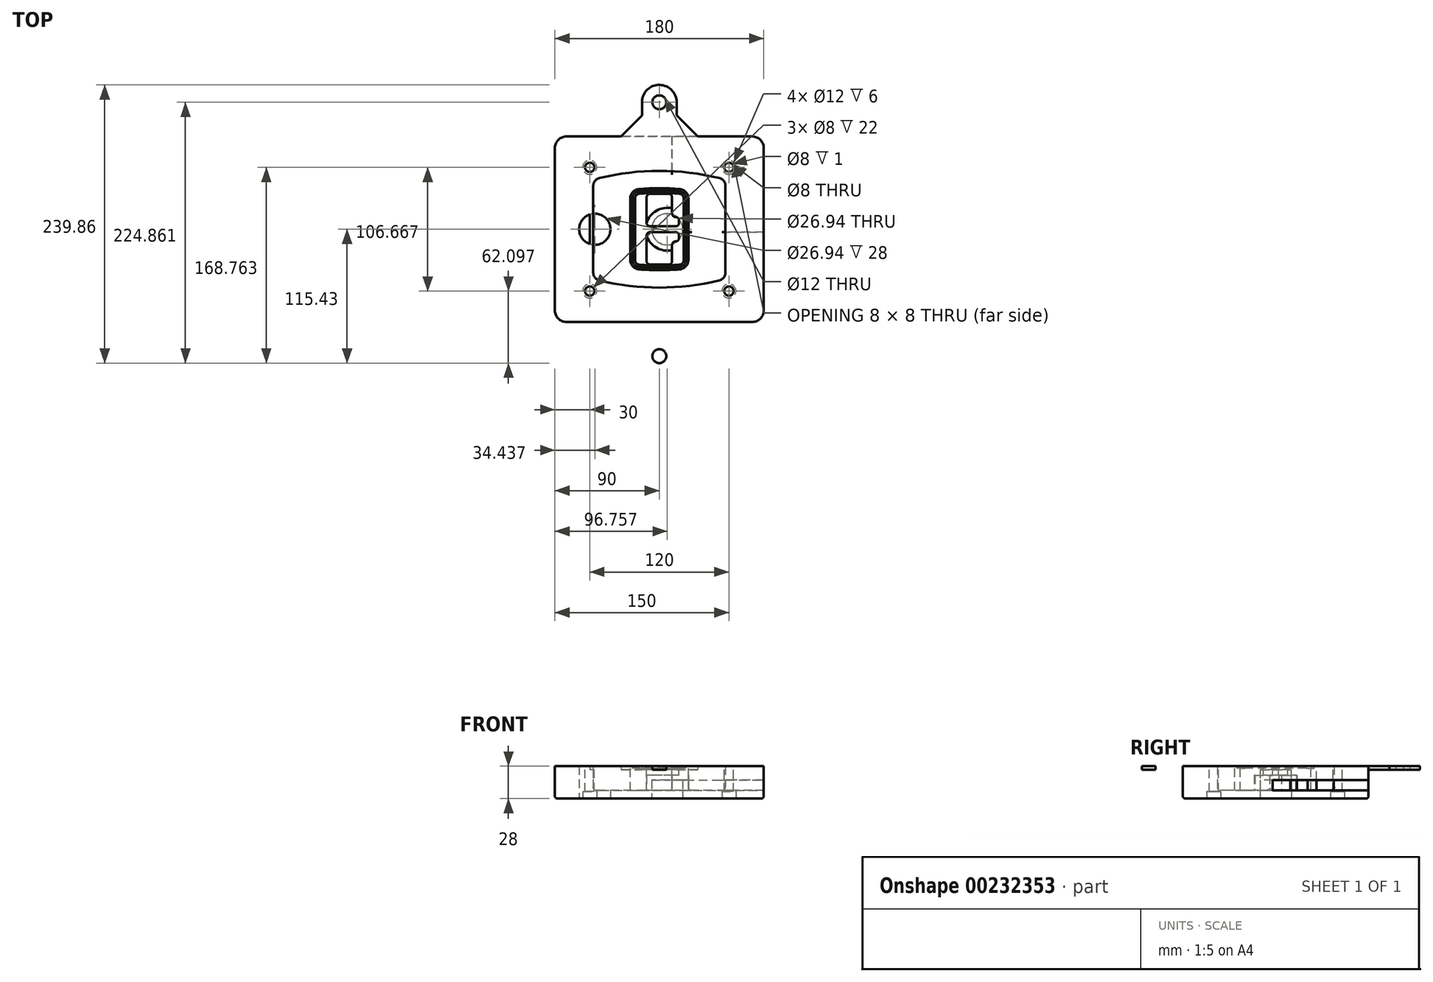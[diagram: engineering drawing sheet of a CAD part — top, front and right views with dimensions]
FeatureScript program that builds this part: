
annotation { "Feature Type Name" : "Feature", "Feature Type Description" : "" }
export const myFeature = defineFeature(function(context is Context, id is Id, definition is map)
    precondition{}
    {
        {
            var Q0;
            Q0=qCreatedBy(makeId("Top.planeOp"),FACE);
            var sketch = newSketch(context, id + "F0", { "sketchPlane" : qUnion([Q0])});
            skPoint(sketch, "E0.rect.middle", {"position": v(0, 0) * mm});
            skLineSegment(sketch, "E1.bottom", {"start": v(-80, -80) * mm, "end": v(80, -80) * mm});
            skLineSegment(sketch, "E1.top", {"start": v(-80, 80) * mm, "end": v(80, 80) * mm});
            skLineSegment(sketch, "E1.left", {"start": v(-90, -70) * mm, "end": v(-90, 70) * mm});
            skLineSegment(sketch, "E1.right", {"start": v(90, -70) * mm, "end": v(90, 70) * mm});
            skLineSegment(sketch, "E2", {"start": v(-90, 80) * mm, "end": v(90, -80) * mm, "construction": true});
            skLineSegment(sketch, "E3", {"start": v(90, 80) * mm, "end": v(-90, -80) * mm, "construction": true});
            skCircle(sketch, "E4", {"center": v(-60, 53.33) * mm, "radius": 4 * mm});
            skCircle(sketch, "E5", {"center": v(60, 53.33) * mm, "radius": 4 * mm});
            skCircle(sketch, "E6", {"center": v(60, -53.33) * mm, "radius": 4 * mm});
            skCircle(sketch, "E7", {"center": v(-60, -53.33) * mm, "radius": 4 * mm});
            skLineSegment(sketch, "E8", {"start": v(-60, 53.33) * mm, "end": v(60, 53.33) * mm, "construction": true});
            skLineSegment(sketch, "E9", {"start": v(60, 53.33) * mm, "end": v(60, -53.33) * mm, "construction": true});
            skLineSegment(sketch, "E10", {"start": v(60, -53.33) * mm, "end": v(-60, -53.33) * mm, "construction": true});
            skLineSegment(sketch, "E11", {"start": v(-60, -53.33) * mm, "end": v(-60, 53.33) * mm, "construction": true});
            skLineSegment(sketch, "E12", {"start": v(-60, 37.3) * mm, "end": v(-60, -37.3) * mm});
            skLineSegment(sketch, "E13", {"start": v(60, 37.3) * mm, "end": v(60, -37.3) * mm});
            skArc(sketch, "E14", {"start": v(52.38, 47.01) * mm, "mid": v(0, 53.33) * mm, "end": v(-52.38, 47.01) * mm});
            skArc(sketch, "E15", {"start": v(-52.38, -47.01) * mm, "mid": v(0, -53.33) * mm, "end": v(52.38, -47.01) * mm});
            skLineSegment(sketch, "E16", {"start": v(-60, 0) * mm, "end": v(60, 0) * mm, "construction": true});
            skPoint(sketch, "E17.visualSharp", {"position": v(-60, -45) * mm});
            skArc(sketch, "E17.filletArc", {"start": v(-60, -37.3) * mm, "mid": v(-57.87, -43.47) * mm, "end": v(-52.38, -47.01) * mm});
            skPoint(sketch, "E18.visualSharp", {"position": v(-60, 45) * mm});
            skArc(sketch, "E18.filletArc", {"start": v(-52.38, 47.01) * mm, "mid": v(-57.87, 43.47) * mm, "end": v(-60, 37.3) * mm});
            skPoint(sketch, "E19.visualSharp", {"position": v(60, 45) * mm});
            skArc(sketch, "E19.filletArc", {"start": v(60, 37.3) * mm, "mid": v(57.87, 43.47) * mm, "end": v(52.38, 47.01) * mm});
            skPoint(sketch, "E20.visualSharp", {"position": v(60, -45) * mm});
            skArc(sketch, "E20.filletArc", {"start": v(52.38, -47.01) * mm, "mid": v(57.87, -43.47) * mm, "end": v(60, -37.3) * mm});
            skPoint(sketch, "E21.visualSharp", {"position": v(-90, 80) * mm});
            skArc(sketch, "E21.filletArc", {"start": v(-80, 80) * mm, "mid": v(-87.07, 77.07) * mm, "end": v(-90, 70) * mm});
            skPoint(sketch, "E22.visualSharp", {"position": v(90, 80) * mm});
            skArc(sketch, "E22.filletArc", {"start": v(90, 70) * mm, "mid": v(87.07, 77.07) * mm, "end": v(80, 80) * mm});
            skPoint(sketch, "E23.visualSharp", {"position": v(90, -80) * mm});
            skArc(sketch, "E23.filletArc", {"start": v(80, -80) * mm, "mid": v(87.07, -77.07) * mm, "end": v(90, -70) * mm});
            skPoint(sketch, "E24.visualSharp", {"position": v(-90, -80) * mm});
            skArc(sketch, "E24.filletArc", {"start": v(-90, -70) * mm, "mid": v(-87.07, -77.07) * mm, "end": v(-80, -80) * mm});
            skArc(sketch, "E25.0", {"start": v(57, 37.3) * mm, "mid": v(55.5, 41.62) * mm, "end": v(51.67, 44.1) * mm});
            skLineSegment(sketch, "E25.1", {"start": v(57, 37.3) * mm, "end": v(57, -37.3) * mm});
            skArc(sketch, "E25.2", {"start": v(51.67, -44.1) * mm, "mid": v(55.5, -41.62) * mm, "end": v(57, -37.3) * mm});
            skArc(sketch, "E25.3", {"start": v(-51.67, -44.1) * mm, "mid": v(0, -50.33) * mm, "end": v(51.67, -44.1) * mm});
            skArc(sketch, "E25.4", {"start": v(-57, -37.3) * mm, "mid": v(-55.5, -41.62) * mm, "end": v(-51.67, -44.1) * mm});
            skArc(sketch, "E25.5", {"start": v(51.67, 44.1) * mm, "mid": v(0, 50.33) * mm, "end": v(-51.67, 44.1) * mm});
            skLineSegment(sketch, "E25.6", {"start": v(-57, 37.3) * mm, "end": v(-57, -37.3) * mm});
            skArc(sketch, "E25.7", {"start": v(-51.67, 44.1) * mm, "mid": v(-55.5, 41.62) * mm, "end": v(-57, 37.3) * mm});
            skArc(sketch, "E26.0", {"start": v(-53.33, 50.9) * mm, "mid": v(-61.01, 45.94) * mm, "end": v(-64, 37.3) * mm});
            skArc(sketch, "E26.1", {"start": v(53.33, 50.9) * mm, "mid": v(0, 57.33) * mm, "end": v(-53.33, 50.9) * mm});
            skArc(sketch, "E26.2", {"start": v(64, 37.3) * mm, "mid": v(61.01, 45.94) * mm, "end": v(53.33, 50.9) * mm});
            skLineSegment(sketch, "E26.3", {"start": v(64, 37.3) * mm, "end": v(64, -37.3) * mm});
            skArc(sketch, "E26.4", {"start": v(53.33, -50.9) * mm, "mid": v(61.01, -45.94) * mm, "end": v(64, -37.3) * mm});
            skLineSegment(sketch, "E26.5", {"start": v(-64, 37.3) * mm, "end": v(-64, -37.3) * mm});
            skArc(sketch, "E26.6", {"start": v(-53.33, -50.9) * mm, "mid": v(0, -57.33) * mm, "end": v(53.33, -50.9) * mm});
            skArc(sketch, "E26.7", {"start": v(-64, -37.3) * mm, "mid": v(-61.01, -45.94) * mm, "end": v(-53.33, -50.9) * mm});
            skSolve(sketch);
        }
        {
            var Q0;
            Q0=makeQuery(id+"F0.imprint","IMPRINT",FACE,{"disambiguationData":[TD([[makeQuery(id+"F0.imprint","IMPRINT",EDGE,{"derivedFrom":sQuery(id+"F0.wireOp",EDGE,"E1.bottom")}),1.0]])]});
            var Q1;
            Q1=makeQuery(id+"F0.imprint","IMPRINT",FACE,{"disambiguationData":[TD([[makeQuery(id+"F0.imprint","IMPRINT",EDGE,{"derivedFrom":sQuery(id+"F0.wireOp",EDGE,"E12")}),1.0]])]});
            var Q2;
            Q2=makeQuery(id+"F0.imprint","IMPRINT",FACE,{"disambiguationData":[TD([[makeQuery(id+"F0.imprint","IMPRINT",EDGE,{"derivedFrom":sQuery(id+"F0.wireOp",EDGE,"E25.0")}),1.0]])]});
            var Q3;
            Q3=makeQuery(id+"F0.imprint","IMPRINT",FACE,{"disambiguationData":[TD([[makeQuery(id+"F0.imprint","IMPRINT",EDGE,{"derivedFrom":sQuery(id+"F0.wireOp",EDGE,"E12")}),-1.0]])]});
            extrude(context, id + "F1", {"entities" : qUnion([Q0, Q1, Q2, Q3]), "oppositeDirection" : true, "depth" : 25 * mm});
        }
        {
            var Q0;
            Q0=makeQuery(id+"F0.imprint","IMPRINT",FACE,{"disambiguationData":[TD([[makeQuery(id+"F0.imprint","IMPRINT",EDGE,{"derivedFrom":sQuery(id+"F0.wireOp",EDGE,"E12")}),1.0]])]});
            extrude(context, id + "F2", {"entities" : qUnion([Q0]), "operationType" : NewBodyOperationType.ADD, "depth" : 3 * mm});
        }
        {
            var Q0;
            Q0=makeQuery(id+"F0.imprint","IMPRINT",FACE,{"disambiguationData":[TD([[makeQuery(id+"F0.imprint","IMPRINT",EDGE,{"derivedFrom":sQuery(id+"F0.wireOp",EDGE,"E25.0")}),1.0]])]});
            extrude(context, id + "F3", {"entities" : qUnion([Q0]), "operationType" : NewBodyOperationType.REMOVE, "oppositeDirection" : true, "depth" : 18 * mm});
        }
        {
            var Q0;
            Q0=makeQuery(id+"F2.opExtrude","CAP_FACE",FACE,{"disambiguationData":[OSD([sQuery(id+"F0.wireOp",EDGE,"E12"),sQuery(id+"F0.wireOp",EDGE,"E13"),sQuery(id+"F0.wireOp",EDGE,"E14"),sQuery(id+"F0.wireOp",EDGE,"E15"),sQuery(id+"F0.wireOp",EDGE,"E17.filletArc"),sQuery(id+"F0.wireOp",EDGE,"E18.filletArc"),sQuery(id+"F0.wireOp",EDGE,"E19.filletArc"),sQuery(id+"F0.wireOp",EDGE,"E20.filletArc"),sQuery(id+"F0.wireOp",EDGE,"E25.0"),sQuery(id+"F0.wireOp",EDGE,"E25.1"),sQuery(id+"F0.wireOp",EDGE,"E25.2"),sQuery(id+"F0.wireOp",EDGE,"E25.3"),sQuery(id+"F0.wireOp",EDGE,"E25.4"),sQuery(id+"F0.wireOp",EDGE,"E25.5"),sQuery(id+"F0.wireOp",EDGE,"E25.6"),sQuery(id+"F0.wireOp",EDGE,"E25.7")])],"isStart":false});
            var sketch = newSketch(context, id + "F4", { "sketchPlane" : qUnion([Q0])});
            skArc(sketch, "E27.0", {"start": v(-17.7, -34.56) * mm, "mid": v(0, -35.33) * mm, "end": v(17.7, -34.56) * mm});
            skArc(sketch, "E28.0", {"start": v(17.7, 34.56) * mm, "mid": v(0, 35.33) * mm, "end": v(-17.7, 34.56) * mm});
            skLineSegment(sketch, "E29", {"start": v(-25, 26.59) * mm, "end": v(-25, -26.59) * mm});
            skLineSegment(sketch, "E30", {"start": v(25, 26.59) * mm, "end": v(25, -26.59) * mm});
            skLineSegment(sketch, "E31", {"start": v(-25, 33.78) * mm, "end": v(25, 33.78) * mm, "construction": true});
            skLineSegment(sketch, "E32", {"start": v(-25, -33.78) * mm, "end": v(25, -33.78) * mm, "construction": true});
            skPoint(sketch, "E33.visualSharp", {"position": v(-25, 33.78) * mm});
            skArc(sketch, "E33.filletArc", {"start": v(-17.7, 34.56) * mm, "mid": v(-22.9, 32) * mm, "end": v(-25, 26.59) * mm});
            skPoint(sketch, "E34.visualSharp", {"position": v(25, 33.78) * mm});
            skArc(sketch, "E34.filletArc", {"start": v(25, 26.59) * mm, "mid": v(22.9, 32) * mm, "end": v(17.7, 34.56) * mm});
            skPoint(sketch, "E35.visualSharp", {"position": v(25, -33.78) * mm});
            skArc(sketch, "E35.filletArc", {"start": v(17.7, -34.56) * mm, "mid": v(22.9, -32) * mm, "end": v(25, -26.59) * mm});
            skPoint(sketch, "E36.visualSharp", {"position": v(-25, -33.78) * mm});
            skArc(sketch, "E36.filletArc", {"start": v(-25, -26.59) * mm, "mid": v(-22.9, -32) * mm, "end": v(-17.7, -34.56) * mm});
            skArc(sketch, "E37.0", {"start": v(51.67, 44.1) * mm, "mid": v(0, 50.33) * mm, "end": v(-51.67, 44.1) * mm});
            skArc(sketch, "E37.1", {"start": v(-51.67, 44.1) * mm, "mid": v(-55.5, 41.62) * mm, "end": v(-57, 37.3) * mm});
            skLineSegment(sketch, "E37.2", {"start": v(-57, 37.3) * mm, "end": v(-57, -37.3) * mm});
            skArc(sketch, "E37.3", {"start": v(-57, -37.3) * mm, "mid": v(-55.5, -41.62) * mm, "end": v(-51.67, -44.1) * mm});
            skArc(sketch, "E37.4", {"start": v(-51.67, -44.1) * mm, "mid": v(0, -50.33) * mm, "end": v(51.67, -44.1) * mm});
            skArc(sketch, "E37.5", {"start": v(51.67, -44.1) * mm, "mid": v(55.5, -41.62) * mm, "end": v(57, -37.3) * mm});
            skLineSegment(sketch, "E37.6", {"start": v(57, 37.3) * mm, "end": v(57, -37.3) * mm});
            skArc(sketch, "E37.7", {"start": v(57, 37.3) * mm, "mid": v(55.5, 41.62) * mm, "end": v(51.67, 44.1) * mm});
            skLineSegment(sketch, "E38.0", {"start": v(23, 26.59) * mm, "end": v(23, -26.59) * mm});
            skArc(sketch, "E38.1", {"start": v(17.53, -32.56) * mm, "mid": v(21.42, -30.64) * mm, "end": v(23, -26.59) * mm});
            skArc(sketch, "E38.2", {"start": v(-17.53, -32.56) * mm, "mid": v(0, -33.33) * mm, "end": v(17.53, -32.56) * mm});
            skArc(sketch, "E38.3", {"start": v(-23, -26.59) * mm, "mid": v(-21.42, -30.64) * mm, "end": v(-17.53, -32.56) * mm});
            skLineSegment(sketch, "E38.4", {"start": v(-23, 26.59) * mm, "end": v(-23, -26.59) * mm});
            skArc(sketch, "E38.5", {"start": v(23, 26.59) * mm, "mid": v(21.42, 30.64) * mm, "end": v(17.53, 32.56) * mm});
            skArc(sketch, "E38.6", {"start": v(-17.53, 32.56) * mm, "mid": v(-21.42, 30.64) * mm, "end": v(-23, 26.59) * mm});
            skArc(sketch, "E38.7", {"start": v(17.53, 32.56) * mm, "mid": v(0, 33.33) * mm, "end": v(-17.53, 32.56) * mm});
            skArc(sketch, "E39.0", {"start": v(21, 26.59) * mm, "mid": v(19.95, 29.29) * mm, "end": v(17.35, 30.57) * mm});
            skLineSegment(sketch, "E39.1", {"start": v(21, 26.59) * mm, "end": v(21, -26.59) * mm});
            skArc(sketch, "E39.2", {"start": v(17.35, -30.57) * mm, "mid": v(19.95, -29.29) * mm, "end": v(21, -26.59) * mm});
            skArc(sketch, "E39.3", {"start": v(-17.35, -30.57) * mm, "mid": v(0, -31.33) * mm, "end": v(17.35, -30.57) * mm});
            skArc(sketch, "E39.4", {"start": v(-21, -26.59) * mm, "mid": v(-19.95, -29.29) * mm, "end": v(-17.35, -30.57) * mm});
            skArc(sketch, "E39.5", {"start": v(17.35, 30.57) * mm, "mid": v(0, 31.33) * mm, "end": v(-17.35, 30.57) * mm});
            skLineSegment(sketch, "E39.6", {"start": v(-21, 26.59) * mm, "end": v(-21, -26.59) * mm});
            skArc(sketch, "E39.7", {"start": v(-17.35, 30.57) * mm, "mid": v(-19.95, 29.29) * mm, "end": v(-21, 26.59) * mm});
            skLineSegment(sketch, "E40", {"start": v(-25, 0) * mm, "end": v(25, 0) * mm, "construction": true});
            skLineSegment(sketch, "E41", {"start": v(-11, 5.5) * mm, "end": v(-11, 27.5) * mm});
            skLineSegment(sketch, "E42", {"start": v(-8, 30.5) * mm, "end": v(8, 30.5) * mm});
            skLineSegment(sketch, "E43", {"start": v(11, 27.5) * mm, "end": v(11, 13.5) * mm});
            skLineSegment(sketch, "E44", {"start": v(14, 10.5) * mm, "end": v(14, 10.5) * mm});
            skLineSegment(sketch, "E45", {"start": v(17, 7.5) * mm, "end": v(17, 5.5) * mm});
            skLineSegment(sketch, "E46", {"start": v(14, 2.5) * mm, "end": v(-8, 2.5) * mm});
            skPoint(sketch, "E47.visualSharp", {"position": v(-11, 30.5) * mm});
            skArc(sketch, "E47.filletArc", {"start": v(-8, 30.5) * mm, "mid": v(-10.12, 29.62) * mm, "end": v(-11, 27.5) * mm});
            skPoint(sketch, "E48.visualSharp", {"position": v(11, 30.5) * mm});
            skArc(sketch, "E48.filletArc", {"start": v(11, 27.5) * mm, "mid": v(10.12, 29.62) * mm, "end": v(8, 30.5) * mm});
            skPoint(sketch, "E49.visualSharp", {"position": v(11, 10.5) * mm});
            skArc(sketch, "E49.filletArc", {"start": v(11, 13.5) * mm, "mid": v(11.88, 11.38) * mm, "end": v(14, 10.5) * mm});
            skPoint(sketch, "E50.visualSharp", {"position": v(17, 10.5) * mm});
            skArc(sketch, "E50.filletArc", {"start": v(17, 7.5) * mm, "mid": v(16.12, 9.62) * mm, "end": v(14, 10.5) * mm});
            skPoint(sketch, "E51.visualSharp", {"position": v(17, 2.5) * mm});
            skArc(sketch, "E51.filletArc", {"start": v(14, 2.5) * mm, "mid": v(16.12, 3.38) * mm, "end": v(17, 5.5) * mm});
            skPoint(sketch, "E52.visualSharp", {"position": v(-11, 2.5) * mm});
            skArc(sketch, "E52.filletArc", {"start": v(-11, 5.5) * mm, "mid": v(-10.12, 3.38) * mm, "end": v(-8, 2.5) * mm});
            skLineSegment(sketch, "E53.0.MirrorCS", {"start": v(14, -2.5) * mm, "end": v(-8, -2.5) * mm});
            skArc(sketch, "E54.0.MirrorCS", {"start": v(-11, -5.5) * mm, "mid": v(-10.12, -3.38) * mm, "end": v(-8, -2.5) * mm});
            skLineSegment(sketch, "E55.0.MirrorCS", {"start": v(-11, -5.5) * mm, "end": v(-11, -27.5) * mm});
            skArc(sketch, "E56.0.MirrorCS", {"start": v(-8, -30.5) * mm, "mid": v(-10.12, -29.62) * mm, "end": v(-11, -27.5) * mm});
            skLineSegment(sketch, "E57.0.MirrorCS", {"start": v(-8, -30.5) * mm, "end": v(8, -30.5) * mm});
            skArc(sketch, "E58.0.MirrorCS", {"start": v(11, -27.5) * mm, "mid": v(10.12, -29.62) * mm, "end": v(8, -30.5) * mm});
            skLineSegment(sketch, "E59.0.MirrorCS", {"start": v(11, -27.5) * mm, "end": v(11, -13.5) * mm});
            skArc(sketch, "E60.0.MirrorCS", {"start": v(11, -13.5) * mm, "mid": v(11.88, -11.38) * mm, "end": v(14, -10.5) * mm});
            skArc(sketch, "E61.0.MirrorCS", {"start": v(17, -7.5) * mm, "mid": v(16.12, -9.62) * mm, "end": v(14, -10.5) * mm});
            skLineSegment(sketch, "E62.0.MirrorCS", {"start": v(17, -7.5) * mm, "end": v(17, -5.5) * mm});
            skArc(sketch, "E63.0.MirrorCS", {"start": v(14, -2.5) * mm, "mid": v(16.12, -3.38) * mm, "end": v(17, -5.5) * mm});
            skSolve(sketch);
        }
        {
            var Q0;
            Q0=makeQuery(id+"F4.imprint","IMPRINT",FACE,{"disambiguationData":[TD([[makeQuery(id+"F4.imprint","IMPRINT",EDGE,{"derivedFrom":sQuery(id+"F4.wireOp",EDGE,"E27.0")}),1.0]])]});
            var Q1;
            Q1=makeQuery(id+"F4.imprint","IMPRINT",FACE,{"disambiguationData":[TD([[makeQuery(id+"F4.imprint","IMPRINT",EDGE,{"derivedFrom":sQuery(id+"F4.wireOp",EDGE,"E38.0")}),-1.0]])]});
            var Q2;
            Q2=makeQuery(id+"F4.imprint","IMPRINT",FACE,{"disambiguationData":[TD([[makeQuery(id+"F4.imprint","IMPRINT",EDGE,{"derivedFrom":sQuery(id+"F4.wireOp",EDGE,"E39.0")}),1.0]])]});
            extrude(context, id + "F5", {"entities" : qUnion([Q0, Q1, Q2]), "operationType" : NewBodyOperationType.ADD, "endBound" : BoundingType.UP_TO_NEXT, "oppositeDirection" : true, "depth" : 25 * mm});
        }
        {
            var Q0;
            Q0=makeQuery(id+"F4.imprint","IMPRINT",FACE,{"disambiguationData":[TD([[makeQuery(id+"F4.imprint","IMPRINT",EDGE,{"derivedFrom":sQuery(id+"F4.wireOp",EDGE,"E38.0")}),-1.0]])]});
            extrude(context, id + "F6", {"entities" : qUnion([Q0]), "operationType" : NewBodyOperationType.REMOVE, "oppositeDirection" : true, "depth" : 2 * mm});
        }
        {
            var Q0;
            Q0=makeQuery(id+"F1.opExtrude","CAP_FACE",FACE,{"disambiguationData":[OSD([sQuery(id+"F0.wireOp",EDGE,"E1.bottom"),sQuery(id+"F0.wireOp",EDGE,"E1.top"),sQuery(id+"F0.wireOp",EDGE,"E1.left"),sQuery(id+"F0.wireOp",EDGE,"E1.right"),sQuery(id+"F0.wireOp",EDGE,"E4"),sQuery(id+"F0.wireOp",EDGE,"E5"),sQuery(id+"F0.wireOp",EDGE,"E6"),sQuery(id+"F0.wireOp",EDGE,"E7"),sQuery(id+"F0.wireOp",EDGE,"E21.filletArc"),sQuery(id+"F0.wireOp",EDGE,"E22.filletArc"),sQuery(id+"F0.wireOp",EDGE,"E23.filletArc"),sQuery(id+"F0.wireOp",EDGE,"E24.filletArc")])],"isStart":false});
            var sketch = newSketch(context, id + "F7", { "sketchPlane" : qUnion([Q0])});
            skCircle(sketch, "E64", {"center": v(6.76, 0) * mm, "radius": 13.47 * mm});
            skCircle(sketch, "E65", {"center": v(-55.56, 0) * mm, "radius": 13.47 * mm});
            skLineSegment(sketch, "E66", {"start": v(90, 0) * mm, "end": v(-90, 0) * mm});
            skCircle(sketch, "E67", {"center": v(6.76, 0) * mm, "radius": 18.47 * mm});
            skCircle(sketch, "E68", {"center": v(60, -53.33) * mm, "radius": 6 * mm});
            skCircle(sketch, "E69", {"center": v(-60, -53.33) * mm, "radius": 6 * mm});
            skCircle(sketch, "E70", {"center": v(-60, 53.33) * mm, "radius": 6 * mm});
            skCircle(sketch, "E71", {"center": v(60, 53.33) * mm, "radius": 6 * mm});
            skSolve(sketch);
        }
        {
            var Q0;
            {var subQ1=sQuery(id+"F7.wireOp",EDGE,"E66");var subQ4=sQuery(id+"F7.wireOp",EDGE,"E64");var subQ6=makeQuery(id+"F7.imprint","INTERSECT",VERTEX,{"disambiguationData":[OD(0.0)],"derivedFrom":[subQ4,subQ1]});Q0=makeQuery(id+"F7.imprint","IMPRINT",FACE,{"disambiguationData":[TD([[makeQuery(id+"F7.imprint","IMPRINT",EDGE,{"disambiguationData":[TD([[subQ6,-1.0]])],"derivedFrom":subQ4}),-1.0]])]});}
            var Q1;
            {var subQ0=sQuery(id+"F7.wireOp",EDGE,"E66");var subQ1=sQuery(id+"F7.wireOp",EDGE,"E64");var subQ3=makeQuery(id+"F7.imprint","INTERSECT",VERTEX,{"disambiguationData":[OD(0.0)],"derivedFrom":[subQ1,subQ0]});Q1=makeQuery(id+"F7.imprint","IMPRINT",FACE,{"disambiguationData":[TD([[makeQuery(id+"F7.imprint","IMPRINT",EDGE,{"disambiguationData":[TD([[subQ3,-1.0]])],"derivedFrom":subQ1}),1.0]])]});}
            var Q2;
            {var subQ0=sQuery(id+"F7.wireOp",EDGE,"E66");var subQ1=sQuery(id+"F7.wireOp",EDGE,"E64");var subQ3=makeQuery(id+"F7.imprint","INTERSECT",VERTEX,{"disambiguationData":[OD(0.0)],"derivedFrom":[subQ1,subQ0]});Q2=makeQuery(id+"F7.imprint","IMPRINT",FACE,{"disambiguationData":[TD([[makeQuery(id+"F7.imprint","IMPRINT",EDGE,{"disambiguationData":[TD([[subQ3,1.0]])],"derivedFrom":subQ1}),1.0]])]});}
            var Q3;
            {var subQ1=sQuery(id+"F7.wireOp",EDGE,"E66");var subQ4=sQuery(id+"F7.wireOp",EDGE,"E64");var subQ6=makeQuery(id+"F7.imprint","INTERSECT",VERTEX,{"disambiguationData":[OD(0.0)],"derivedFrom":[subQ4,subQ1]});Q3=makeQuery(id+"F7.imprint","IMPRINT",FACE,{"disambiguationData":[TD([[makeQuery(id+"F7.imprint","IMPRINT",EDGE,{"disambiguationData":[TD([[subQ6,1.0]])],"derivedFrom":subQ4}),-1.0]])]});}
            extrude(context, id + "F8", {"entities" : qUnion([Q0, Q1, Q2, Q3]), "operationType" : NewBodyOperationType.ADD, "oppositeDirection" : true, "depth" : 20 * mm});
        }
        {
            var Q0;
            {var subQ0=sQuery(id+"F7.wireOp",EDGE,"E66");var subQ1=sQuery(id+"F7.wireOp",EDGE,"E64");var subQ3=makeQuery(id+"F7.imprint","INTERSECT",VERTEX,{"disambiguationData":[OD(0.0)],"derivedFrom":[subQ1,subQ0]});Q0=makeQuery(id+"F7.imprint","IMPRINT",FACE,{"disambiguationData":[TD([[makeQuery(id+"F7.imprint","IMPRINT",EDGE,{"disambiguationData":[TD([[subQ3,-1.0]])],"derivedFrom":subQ1}),1.0]])]});}
            var Q1;
            {var subQ0=sQuery(id+"F7.wireOp",EDGE,"E66");var subQ1=sQuery(id+"F7.wireOp",EDGE,"E64");var subQ3=makeQuery(id+"F7.imprint","INTERSECT",VERTEX,{"disambiguationData":[OD(0.0)],"derivedFrom":[subQ1,subQ0]});Q1=makeQuery(id+"F7.imprint","IMPRINT",FACE,{"disambiguationData":[TD([[makeQuery(id+"F7.imprint","IMPRINT",EDGE,{"disambiguationData":[TD([[subQ3,1.0]])],"derivedFrom":subQ1}),1.0]])]});}
            extrude(context, id + "F9", {"entities" : qUnion([Q0, Q1]), "operationType" : NewBodyOperationType.REMOVE, "oppositeDirection" : true, "depth" : 16 * mm});
        }
        {
            var Q0;
            {var subQ0=sQuery(id+"F7.wireOp",EDGE,"E66");var subQ1=sQuery(id+"F7.wireOp",EDGE,"E65");var subQ3=makeQuery(id+"F7.imprint","INTERSECT",VERTEX,{"disambiguationData":[OD(0.0)],"derivedFrom":[subQ1,subQ0]});Q0=makeQuery(id+"F7.imprint","IMPRINT",FACE,{"disambiguationData":[TD([[makeQuery(id+"F7.imprint","IMPRINT",EDGE,{"disambiguationData":[TD([[subQ3,-1.0]])],"derivedFrom":subQ1}),1.0]])]});}
            var Q1;
            {var subQ0=sQuery(id+"F7.wireOp",EDGE,"E66");var subQ1=sQuery(id+"F7.wireOp",EDGE,"E65");var subQ3=makeQuery(id+"F7.imprint","INTERSECT",VERTEX,{"disambiguationData":[OD(0.0)],"derivedFrom":[subQ1,subQ0]});Q1=makeQuery(id+"F7.imprint","IMPRINT",FACE,{"disambiguationData":[TD([[makeQuery(id+"F7.imprint","IMPRINT",EDGE,{"disambiguationData":[TD([[subQ3,1.0]])],"derivedFrom":subQ1}),1.0]])]});}
            extrude(context, id + "F10", {"entities" : qUnion([Q0, Q1]), "operationType" : NewBodyOperationType.REMOVE, "oppositeDirection" : true, "depth" : 25 * mm});
        }
        {
            var Q0;
            Q0=makeQuery(id+"F7.imprint","IMPRINT",FACE,{"disambiguationData":[TD([[makeQuery(id+"F7.imprint","IMPRINT",EDGE,{"derivedFrom":sQuery(id+"F7.wireOp",EDGE,"E68")}),1.0]])]});
            var Q1;
            Q1=makeQuery(id+"F7.imprint","IMPRINT",FACE,{"disambiguationData":[TD([[makeQuery(id+"F7.imprint","IMPRINT",EDGE,{"derivedFrom":makeQuery(id+"F1.opExtrude","CAP_EDGE",EDGE,{"disambiguationData":[OSD([sQuery(id+"F0.wireOp",EDGE,"E5")])],"isStart":false})}),-1.0]])]});
            var Q2;
            Q2=makeQuery(id+"F7.imprint","IMPRINT",FACE,{"disambiguationData":[TD([[makeQuery(id+"F7.imprint","IMPRINT",EDGE,{"derivedFrom":sQuery(id+"F7.wireOp",EDGE,"E69")}),1.0]])]});
            var Q3;
            Q3=makeQuery(id+"F7.imprint","IMPRINT",FACE,{"disambiguationData":[TD([[makeQuery(id+"F7.imprint","IMPRINT",EDGE,{"derivedFrom":makeQuery(id+"F1.opExtrude","CAP_EDGE",EDGE,{"disambiguationData":[OSD([sQuery(id+"F0.wireOp",EDGE,"E4")])],"isStart":false})}),-1.0]])]});
            var Q4;
            Q4=makeQuery(id+"F7.imprint","IMPRINT",FACE,{"disambiguationData":[TD([[makeQuery(id+"F7.imprint","IMPRINT",EDGE,{"derivedFrom":sQuery(id+"F7.wireOp",EDGE,"E70")}),1.0]])]});
            var Q5;
            Q5=makeQuery(id+"F7.imprint","IMPRINT",FACE,{"disambiguationData":[TD([[makeQuery(id+"F7.imprint","IMPRINT",EDGE,{"derivedFrom":makeQuery(id+"F1.opExtrude","CAP_EDGE",EDGE,{"disambiguationData":[OSD([sQuery(id+"F0.wireOp",EDGE,"E7")])],"isStart":false})}),-1.0]])]});
            var Q6;
            Q6=makeQuery(id+"F7.imprint","IMPRINT",FACE,{"disambiguationData":[TD([[makeQuery(id+"F7.imprint","IMPRINT",EDGE,{"derivedFrom":sQuery(id+"F7.wireOp",EDGE,"E71")}),1.0]])]});
            var Q7;
            Q7=makeQuery(id+"F7.imprint","IMPRINT",FACE,{"disambiguationData":[TD([[makeQuery(id+"F7.imprint","IMPRINT",EDGE,{"derivedFrom":makeQuery(id+"F1.opExtrude","CAP_EDGE",EDGE,{"disambiguationData":[OSD([sQuery(id+"F0.wireOp",EDGE,"E6")])],"isStart":false})}),-1.0]])]});
            extrude(context, id + "F11", {"entities" : qUnion([Q0, Q1, Q2, Q3, Q4, Q5, Q6, Q7]), "operationType" : NewBodyOperationType.REMOVE, "oppositeDirection" : true, "depth" : 6 * mm});
        }
        {
            var Q0;
            Q0=makeQuery(id+"F9.boolean.opBoolean","COPY",FACE,{"derivedFrom":makeQuery(id+"F9.opExtrude","CAP_FACE",FACE,{"disambiguationData":[OSD([sQuery(id+"F7.wireOp",EDGE,"E64")])],"isStart":false})});
            var sketch = newSketch(context, id + "F12", { "sketchPlane" : qUnion([Q0])});
            skArc(sketch, "E72.0", {"start": v(11, -88.19) * mm, "mid": v(97.1, -83.6) * mm, "end": v(92.5, 2.5) * mm});
            skLineSegment(sketch, "E72.1", {"start": v(11, -17.97) * mm, "end": v(11, -17.97) * mm});
            skLineSegment(sketch, "E73", {"start": v(92.5, -105.13) * mm, "end": v(102.3, -105.13) * mm});
            skLineSegment(sketch, "E74.0", {"start": v(92.5, 2.5) * mm, "end": v(14, 2.5) * mm});
            skArc(sketch, "E74.1", {"start": v(14, 2.5) * mm, "mid": v(16.12, 3.38) * mm, "end": v(17, 5.5) * mm});
            skLineSegment(sketch, "E74.2", {"start": v(17, 7.5) * mm, "end": v(17, 5.5) * mm});
            skArc(sketch, "E74.3", {"start": v(17, 7.5) * mm, "mid": v(16.12, 9.62) * mm, "end": v(14, 10.5) * mm});
            skArc(sketch, "E74.4", {"start": v(11, 13.5) * mm, "mid": v(11.88, 11.38) * mm, "end": v(14, 10.5) * mm});
            skLineSegment(sketch, "E74.5", {"start": v(11, 13.5) * mm, "end": v(11, -88.19) * mm});
            skLineSegment(sketch, "E74.7", {"start": v(92.5, -2.5) * mm, "end": v(14, -2.5) * mm});
            skArc(sketch, "E74.8", {"start": v(14, -2.5) * mm, "mid": v(16.12, -3.38) * mm, "end": v(17, -5.5) * mm});
            skLineSegment(sketch, "E74.9", {"start": v(17, -7.5) * mm, "end": v(17, -5.5) * mm});
            skArc(sketch, "E74.10", {"start": v(17, -7.5) * mm, "mid": v(16.12, -9.62) * mm, "end": v(14, -10.5) * mm});
            skArc(sketch, "E74.11", {"start": v(11, -13.5) * mm, "mid": v(11.88, -11.38) * mm, "end": v(14, -10.5) * mm});
            skLineSegment(sketch, "E74.12", {"start": v(11, -17.97) * mm, "end": v(11, -13.5) * mm});
            skPoint(sketch, "E75.orphan", {"position": v(11, -27.5) * mm});
            skPoint(sketch, "E76.orphan", {"position": v(-8, -2.5) * mm});
            skPoint(sketch, "E77.orphan", {"position": v(-8, 2.5) * mm});
            skPoint(sketch, "E78.orphan", {"position": v(11, 27.5) * mm});
            skSolve(sketch);
        }
        {
            var Q0;
            {var subQ7=sQuery(id+"F12.wireOp",EDGE,"E72.0");var subQ14=sQuery(id+"F12.wireOp",EDGE,"E72.1");var subQ16=sQuery(id+"F12.wireOp",EDGE,"E74.1");var subQ18=sQuery(id+"F12.wireOp",EDGE,"E74.8");Q0=qUnion([makeQuery(id+"F12.imprint","IMPRINT",FACE,{"disambiguationData":[TD([[makeQuery(id+"F12.imprint","IMPRINT",EDGE,{"derivedFrom":subQ7}),1.0]])]}),makeQuery(id+"F12.imprint","IMPRINT",FACE,{"disambiguationData":[TD([[makeQuery(id+"F12.imprint","IMPRINT",EDGE,{"derivedFrom":subQ14}),1.0]])]}),makeQuery(id+"F12.imprint","IMPRINT",FACE,{"disambiguationData":[TD([[makeQuery(id+"F12.imprint","IMPRINT",EDGE,{"derivedFrom":subQ16}),1.0]])]}),makeQuery(id+"F12.imprint","IMPRINT",FACE,{"disambiguationData":[TD([[makeQuery(id+"F12.imprint","IMPRINT",EDGE,{"derivedFrom":subQ18}),-1.0]])]})]);}
            var Q1;
            Q1=makeQuery(id+"F5.boolean.opBoolean","SPLIT",FACE,{"disambiguationData":[TD([makeQuery(id+"F5.opExtrude","SWEPT_FACE",FACE,{"disambiguationData":[OSD([sQuery(id+"F4.wireOp",EDGE,"E41")])]})])],"derivedFrom":makeQuery(id+"F3.boolean.opBoolean","COPY",FACE,{"derivedFrom":makeQuery(id+"F3.opExtrude","CAP_FACE",FACE,{"disambiguationData":[OSD([sQuery(id+"F0.wireOp",EDGE,"E25.0"),sQuery(id+"F0.wireOp",EDGE,"E25.1"),sQuery(id+"F0.wireOp",EDGE,"E25.2"),sQuery(id+"F0.wireOp",EDGE,"E25.3"),sQuery(id+"F0.wireOp",EDGE,"E25.4"),sQuery(id+"F0.wireOp",EDGE,"E25.5"),sQuery(id+"F0.wireOp",EDGE,"E25.6"),sQuery(id+"F0.wireOp",EDGE,"E25.7")])],"isStart":false})})});
            extrude(context, id + "F13", {"entities" : qUnion([Q0]), "operationType" : NewBodyOperationType.REMOVE, "endBound" : BoundingType.UP_TO_SURFACE, "endBoundEntityFace" : qUnion([Q1]), "depth" : 25 * mm});
        }
        {
            var Q0;
            Q0=makeQuery(id+"F3.boolean.opBoolean","COPY",EDGE,{"derivedFrom":makeQuery(id+"F3.opExtrude","CAP_EDGE",EDGE,{"disambiguationData":[OSD([sQuery(id+"F0.wireOp",EDGE,"E25.6")])],"isStart":false})});
            var Q1;
            Q1=makeQuery(id+"F8.boolean.opBoolean","INTERSECT",EDGE,{"derivedFrom":[makeQuery(id+"F5.opExtrude","SWEPT_FACE",FACE,{"disambiguationData":[OSD([sQuery(id+"F4.wireOp",EDGE,"E30")])]}),makeQuery(id+"F8.opExtrude","CAP_FACE",FACE,{"disambiguationData":[OSD([sQuery(id+"F7.wireOp",EDGE,"E67")])],"isStart":false})]});
            var Q2;
            Q2=makeQuery(id+"F8.boolean.opBoolean","INTERSECT",EDGE,{"disambiguationData":[OD(1.0)],"derivedFrom":[makeQuery(id+"F5.opExtrude","SWEPT_FACE",FACE,{"disambiguationData":[OSD([sQuery(id+"F4.wireOp",EDGE,"E30")])]}),makeQuery(id+"F8.opExtrude","SWEPT_FACE",FACE,{"disambiguationData":[OSD([sQuery(id+"F7.wireOp",EDGE,"E67")])]})]});
            var Q3;
            {var subQ0=makeQuery(id+"F3.boolean.opBoolean","COPY",FACE,{"derivedFrom":makeQuery(id+"F3.opExtrude","CAP_FACE",FACE,{"disambiguationData":[OSD([sQuery(id+"F0.wireOp",EDGE,"E25.0"),sQuery(id+"F0.wireOp",EDGE,"E25.1"),sQuery(id+"F0.wireOp",EDGE,"E25.2"),sQuery(id+"F0.wireOp",EDGE,"E25.3"),sQuery(id+"F0.wireOp",EDGE,"E25.4"),sQuery(id+"F0.wireOp",EDGE,"E25.5"),sQuery(id+"F0.wireOp",EDGE,"E25.6"),sQuery(id+"F0.wireOp",EDGE,"E25.7")])],"isStart":false})});var subQ1=sQuery(id+"F4.wireOp",EDGE,"E30");Q3=makeQuery(id+"F8.boolean.opBoolean","SPLIT",EDGE,{"disambiguationData":[TD([makeQuery(id+"F5.opExtrude","SWEPT_FACE",FACE,{"disambiguationData":[OSD([sQuery(id+"F4.wireOp",EDGE,"E35.filletArc")])]})])],"derivedFrom":makeQuery(id+"F5.opExtrude","TWEAK_EDGE",EDGE,{"derivedFrom":[subQ0,makeQuery(id+"F4.imprint","IMPRINT",EDGE,{"derivedFrom":subQ1})]})});}
            var Q4;
            {var subQ0=sQuery(id+"F0.wireOp",EDGE,"E25.0");var subQ1=sQuery(id+"F0.wireOp",EDGE,"E25.1");var subQ2=sQuery(id+"F0.wireOp",EDGE,"E25.2");var subQ3=sQuery(id+"F0.wireOp",EDGE,"E25.3");var subQ4=sQuery(id+"F0.wireOp",EDGE,"E25.4");var subQ5=sQuery(id+"F0.wireOp",EDGE,"E25.5");var subQ6=sQuery(id+"F0.wireOp",EDGE,"E25.6");var subQ7=sQuery(id+"F0.wireOp",EDGE,"E25.7");Q4=makeQuery(id+"F8.boolean.opBoolean","INTERSECT",EDGE,{"derivedFrom":[makeQuery(id+"F5.boolean.opBoolean","SPLIT",FACE,{"disambiguationData":[TD([makeQuery(id+"F2.opExtrude","SWEPT_FACE",FACE,{"disambiguationData":[OSD([subQ0])]})])],"derivedFrom":makeQuery(id+"F3.boolean.opBoolean","COPY",FACE,{"derivedFrom":makeQuery(id+"F3.opExtrude","CAP_FACE",FACE,{"disambiguationData":[OSD([subQ0,subQ1,subQ2,subQ3,subQ4,subQ5,subQ6,subQ7])],"isStart":false})})}),makeQuery(id+"F8.opExtrude","SWEPT_FACE",FACE,{"disambiguationData":[OSD([sQuery(id+"F7.wireOp",EDGE,"E67")])]})]});}
            var Q5;
            Q5=makeQuery(id+"F8.boolean.opBoolean","INTERSECT",EDGE,{"disambiguationData":[OD(0.0)],"derivedFrom":[makeQuery(id+"F5.opExtrude","SWEPT_FACE",FACE,{"disambiguationData":[OSD([sQuery(id+"F4.wireOp",EDGE,"E30")])]}),makeQuery(id+"F8.opExtrude","SWEPT_FACE",FACE,{"disambiguationData":[OSD([sQuery(id+"F7.wireOp",EDGE,"E67")])]})]});
            fillet(context, id + "F14", {"entities" : qUnion([Q0, Q1, Q2, Q3, Q4, Q5]), "radius" : 3 * mm, "tangentPropagation" : true, "allowEdgeOverflow" : false});
        }
        {
            var Q0;
            Q0=makeQuery(id+"F1.opExtrude","CAP_EDGE",EDGE,{"disambiguationData":[OSD([sQuery(id+"F0.wireOp",EDGE,"E1.bottom")])],"isStart":false});
            fillet(context, id + "F15", {"entities" : qUnion([Q0]), "radius" : 2 * mm, "tangentPropagation" : true, "allowEdgeOverflow" : false});
        }
        {
            var Q0;
            {var subQ0=sQuery(id+"F0.wireOp",EDGE,"E22.filletArc");var subQ1=sQuery(id+"F0.wireOp",EDGE,"E7");var subQ2=sQuery(id+"F0.wireOp",EDGE,"E6");var subQ3=sQuery(id+"F0.wireOp",EDGE,"E5");var subQ4=sQuery(id+"F0.wireOp",EDGE,"E4");var subQ5=sQuery(id+"F0.wireOp",EDGE,"E1.bottom");var subQ6=sQuery(id+"F0.wireOp",EDGE,"E21.filletArc");var subQ7=sQuery(id+"F0.wireOp",EDGE,"E1.top");var subQ8=sQuery(id+"F0.wireOp",EDGE,"E1.left");var subQ9=sQuery(id+"F0.wireOp",EDGE,"E1.right");var subQ10=sQuery(id+"F0.wireOp",EDGE,"E23.filletArc");var subQ11=sQuery(id+"F0.wireOp",EDGE,"E24.filletArc");Q0=makeQuery(id+"F2.boolean.opBoolean","SPLIT",FACE,{"disambiguationData":[TD([makeQuery(id+"F1.opExtrude","SWEPT_FACE",FACE,{"disambiguationData":[OSD([subQ5])]})])],"derivedFrom":makeQuery(id+"F1.opExtrude","CAP_FACE",FACE,{"disambiguationData":[OSD([subQ5,subQ7,subQ8,subQ9,subQ4,subQ3,subQ2,subQ1,subQ6,subQ0,subQ10,subQ11])],"isStart":true})});}
            var sketch = newSketch(context, id + "F16", { "sketchPlane" : qUnion([Q0])});
            skArc(sketch, "E79.2", {"start": v(52.38, 47.01) * mm, "mid": v(0, 53.33) * mm, "end": v(-52.38, 47.01) * mm});
            skLineSegment(sketch, "E79.3", {"start": v(60, 37.3) * mm, "end": v(60, -37.3) * mm});
            skArc(sketch, "E79.4", {"start": v(-52.38, -47.01) * mm, "mid": v(0, -53.33) * mm, "end": v(52.38, -47.01) * mm});
            skArc(sketch, "E79.5", {"start": v(-60, -37.3) * mm, "mid": v(-57.87, -43.47) * mm, "end": v(-52.38, -47.01) * mm});
            skArc(sketch, "E79.6", {"start": v(52.38, -47.01) * mm, "mid": v(57.87, -43.47) * mm, "end": v(60, -37.3) * mm});
            skArc(sketch, "E79.7", {"start": v(-52.38, 47.01) * mm, "mid": v(-57.87, 43.47) * mm, "end": v(-60, 37.3) * mm});
            skArc(sketch, "E79.8", {"start": v(60, 37.3) * mm, "mid": v(57.87, 43.47) * mm, "end": v(52.38, 47.01) * mm});
            skLineSegment(sketch, "E79.9", {"start": v(90, -70) * mm, "end": v(90, 70) * mm});
            skArc(sketch, "E79.10", {"start": v(90, 70) * mm, "mid": v(87.07, 77.07) * mm, "end": v(80, 80) * mm});
            skLineSegment(sketch, "E79.11", {"start": v(-80, 80) * mm, "end": v(80, 80) * mm});
            skArc(sketch, "E79.12", {"start": v(-80, 80) * mm, "mid": v(-87.07, 77.07) * mm, "end": v(-90, 70) * mm});
            skArc(sketch, "E79.13", {"start": v(-90, -70) * mm, "mid": v(-87.07, -77.07) * mm, "end": v(-80, -80) * mm});
            skLineSegment(sketch, "E79.14", {"start": v(-80, -80) * mm, "end": v(80, -80) * mm});
            skCircle(sketch, "E79.15", {"center": v(-60, -53.33) * mm, "radius": 4 * mm});
            skCircle(sketch, "E79.16", {"center": v(60, -53.33) * mm, "radius": 4 * mm});
            skArc(sketch, "E79.17", {"start": v(80, -80) * mm, "mid": v(87.07, -77.07) * mm, "end": v(90, -70) * mm});
            skCircle(sketch, "E79.18", {"center": v(-60, 53.33) * mm, "radius": 4 * mm});
            skCircle(sketch, "E79.19", {"center": v(60, 53.33) * mm, "radius": 4 * mm});
            skPoint(sketch, "E80.endSnap0", {"position": v(0, 80) * mm});
            skLineSegment(sketch, "E81", {"start": v(-32.99, 80) * mm, "end": v(-14.99, 98) * mm});
            skLineSegment(sketch, "E82", {"start": v(-14.99, 110) * mm, "end": v(-14.99, 98) * mm});
            skLineSegment(sketch, "E83", {"start": v(15, 109.43) * mm, "end": v(15, 98) * mm});
            skLineSegment(sketch, "E84", {"start": v(15, 98) * mm, "end": v(33, 80) * mm});
            skArc(sketch, "E85", {"start": v(15, 109.43) * mm, "mid": v(0.28, 124.43) * mm, "end": v(-14.99, 110) * mm});
            skLineSegment(sketch, "E86", {"start": v(0, 109.43) * mm, "end": v(0, 80) * mm});
            skCircle(sketch, "E87", {"center": v(0, 109.43) * mm, "radius": 6 * mm});
            skLineSegment(sketch, "E88", {"start": v(0, 0) * mm, "end": v(-90, 0) * mm});
            skLineSegment(sketch, "E89", {"start": v(0, 0) * mm, "end": v(90, 0) * mm});
            skLineSegment(sketch, "E90.MirrorCS", {"start": v(0, -109.43) * mm, "end": v(0, -80) * mm});
            skCircle(sketch, "E91.MirrorC", {"center": v(0, -109.43) * mm, "radius": 6 * mm});
            skLineSegment(sketch, "E92.MirrorCS", {"start": v(-14.99, -110) * mm, "end": v(-14.99, -98) * mm});
            skLineSegment(sketch, "E93.MirrorCS", {"start": v(15, -109.43) * mm, "end": v(15, -98) * mm});
            skArc(sketch, "E94.MirrorCS", {"start": v(15, -109.43) * mm, "mid": v(0.28, -124.43) * mm, "end": v(-14.99, -110) * mm});
            skLineSegment(sketch, "E95.MirrorCS", {"start": v(15, -98) * mm, "end": v(33, -80) * mm});
            skLineSegment(sketch, "E96.MirrorCS", {"start": v(-32.99, -80) * mm, "end": v(-14.99, -98) * mm});
            skSolve(sketch);
        }
        {
            var Q0;
            {var subQ0=sQuery(id+"F16.wireOp",EDGE,"E81");Q0=makeQuery(id+"F16.imprint","IMPRINT",FACE,{"disambiguationData":[TD([[makeQuery(id+"F16.imprint","IMPRINT",EDGE,{"derivedFrom":subQ0}),-1.0]])]});}
            var Q1;
            Q1=makeQuery(id+"F16.imprint","IMPRINT",FACE,{"disambiguationData":[TD([[makeQuery(id+"F16.imprint","IMPRINT",EDGE,{"derivedFrom":sQuery(id+"F16.wireOp",EDGE,"E79.2")}),-1.0]])]});
            var Q2;
            Q2=makeQuery(id+"F16.imprint","IMPRINT",FACE,{"disambiguationData":[TD([[makeQuery(id+"F16.imprint","IMPRINT",EDGE,{"derivedFrom":sQuery(id+"F16.wireOp",EDGE,"E79.4")}),-1.0]])]});
            var Q3;
            Q3=makeQuery(id+"F16.imprint","IMPRINT",FACE,{"disambiguationData":[TD([[makeQuery(id+"F16.imprint","IMPRINT",EDGE,{"derivedFrom":sQuery(id+"F16.wireOp",EDGE,"E91.MirrorC")}),1.0]])]});
            var Q4;
            Q4=makeQuery(id+"F2.opExtrude","CAP_FACE",FACE,{"disambiguationData":[OSD([sQuery(id+"F0.wireOp",EDGE,"E12"),sQuery(id+"F0.wireOp",EDGE,"E13"),sQuery(id+"F0.wireOp",EDGE,"E14"),sQuery(id+"F0.wireOp",EDGE,"E15"),sQuery(id+"F0.wireOp",EDGE,"E17.filletArc"),sQuery(id+"F0.wireOp",EDGE,"E18.filletArc"),sQuery(id+"F0.wireOp",EDGE,"E19.filletArc"),sQuery(id+"F0.wireOp",EDGE,"E20.filletArc"),sQuery(id+"F0.wireOp",EDGE,"E25.0"),sQuery(id+"F0.wireOp",EDGE,"E25.1"),sQuery(id+"F0.wireOp",EDGE,"E25.2"),sQuery(id+"F0.wireOp",EDGE,"E25.3"),sQuery(id+"F0.wireOp",EDGE,"E25.4"),sQuery(id+"F0.wireOp",EDGE,"E25.5"),sQuery(id+"F0.wireOp",EDGE,"E25.6"),sQuery(id+"F0.wireOp",EDGE,"E25.7")])],"isStart":false});
            extrude(context, id + "F17", {"entities" : qUnion([Q0, Q1, Q2, Q3]), "operationType" : NewBodyOperationType.ADD, "endBound" : BoundingType.UP_TO_SURFACE, "endBoundEntityFace" : qUnion([Q4]), "depth" : 25 * mm});
        }
    });
